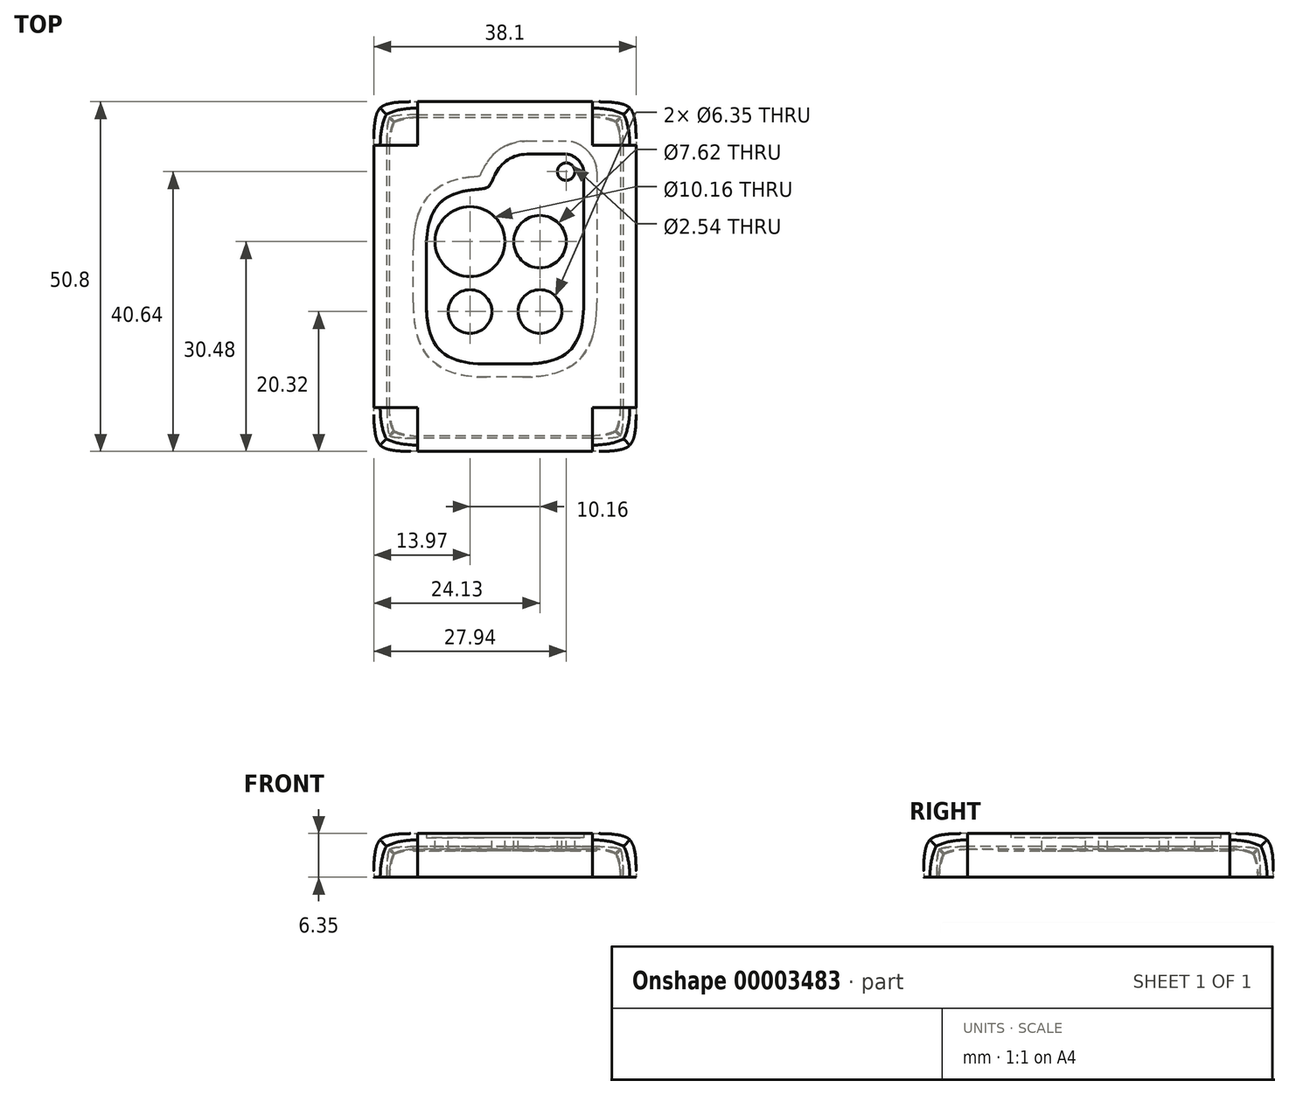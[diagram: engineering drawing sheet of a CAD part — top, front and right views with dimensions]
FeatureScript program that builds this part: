
annotation { "Feature Type Name" : "Feature", "Feature Type Description" : "" }
export const myFeature = defineFeature(function(context is Context, id is Id, definition is map)
    precondition{}
    {
        {
            var Q0;
            Q0=qCreatedBy(makeId("Top.planeOp"),FACE);
            var sketch = newSketch(context, id + "F0", { "sketchPlane" : qUnion([Q0])});
            skLineSegment(sketch, "E0.rect.bottom", {"start": v(19.05, 25.4) * mm, "end": v(-19.05, 25.4) * mm});
            skLineSegment(sketch, "E0.rect.top", {"start": v(19.05, -25.4) * mm, "end": v(-19.05, -25.4) * mm});
            skLineSegment(sketch, "E0.rect.left", {"start": v(19.05, 25.4) * mm, "end": v(19.05, -25.4) * mm});
            skLineSegment(sketch, "E0.rect.right", {"start": v(-19.05, 25.4) * mm, "end": v(-19.05, -25.4) * mm});
            skPoint(sketch, "E0.rect.middle", {"position": v(0, 0) * mm});
            skSolve(sketch);
        }
        {
            var Q0;
            Q0 = qSketchRegion(id + "F0", true);
            extrude(context, id + "F1", {"entities" : qUnion([Q0]), "depth" : 6.35 * mm});
        }
        {
            var Q0;
            Q0=makeQuery(id+"F1.opExtrude","SWEPT_EDGE",EDGE,{"disambiguationData":[OSD([sQuery(id+"F0.wireOp",EDGE,"E0.rect.top"),sQuery(id+"F0.wireOp",EDGE,"E0.rect.right")])]});
            var Q1;
            Q1=makeQuery(id+"F1.opExtrude","SWEPT_EDGE",EDGE,{"disambiguationData":[OSD([sQuery(id+"F0.wireOp",EDGE,"E0.rect.top"),sQuery(id+"F0.wireOp",EDGE,"E0.rect.left")])]});
            var Q2;
            Q2=makeQuery(id+"F1.opExtrude","SWEPT_EDGE",EDGE,{"disambiguationData":[OSD([sQuery(id+"F0.wireOp",EDGE,"E0.rect.bottom"),sQuery(id+"F0.wireOp",EDGE,"E0.rect.left")])]});
            var Q3;
            Q3=makeQuery(id+"F1.opExtrude","SWEPT_EDGE",EDGE,{"disambiguationData":[OSD([sQuery(id+"F0.wireOp",EDGE,"E0.rect.bottom"),sQuery(id+"F0.wireOp",EDGE,"E0.rect.right")])]});
            var Q4;
            Q4=makeQuery(id+"F1.opExtrude","CAP_FACE",FACE,{"disambiguationData":[OSD([sQuery(id+"F0.wireOp",EDGE,"E0.rect.bottom"),sQuery(id+"F0.wireOp",EDGE,"E0.rect.top"),sQuery(id+"F0.wireOp",EDGE,"E0.rect.left"),sQuery(id+"F0.wireOp",EDGE,"E0.rect.right")])],"isStart":false});
            fillet(context, id + "F2", {"entities" : qUnion([Q0, Q1, Q2, Q3, Q4]), "radius" : 6.35 * mm, "tangentPropagation" : true, "rho" : 0.71, "crossSection" : FilletCrossSection.CONIC, "allowEdgeOverflow" : false});
        }
        {
            var Q0;
            Q0=makeQuery(id+"F1.opExtrude","CAP_FACE",FACE,{"disambiguationData":[OSD([sQuery(id+"F0.wireOp",EDGE,"E0.rect.bottom"),sQuery(id+"F0.wireOp",EDGE,"E0.rect.top"),sQuery(id+"F0.wireOp",EDGE,"E0.rect.left"),sQuery(id+"F0.wireOp",EDGE,"E0.rect.right")])],"isStart":false});
            var sketch = newSketch(context, id + "F3", { "sketchPlane" : qUnion([Q0])});
            skLineSegment(sketch, "E1.rect.bottom", {"start": v(-1.9, 12.7) * mm, "end": v(-11.43, 12.7) * mm});
            skLineSegment(sketch, "E1.rect.top", {"start": v(11.43, -12.7) * mm, "end": v(-11.43, -12.7) * mm});
            skLineSegment(sketch, "E1.rect.left", {"start": v(11.43, 12.7) * mm, "end": v(11.43, -12.7) * mm});
            skLineSegment(sketch, "E1.rect.right", {"start": v(-11.43, 12.7) * mm, "end": v(-11.43, -12.7) * mm});
            skPoint(sketch, "E1.rect.middle", {"position": v(0, 0) * mm});
            skArc(sketch, "E2", {"start": v(3.17, 17.78) * mm, "mid": v(-0.42, 16.3) * mm, "end": v(-1.9, 12.7) * mm});
            skLineSegment(sketch, "E3", {"start": v(11.43, 12.7) * mm, "end": v(11.43, 17.78) * mm});
            skLineSegment(sketch, "E4", {"start": v(11.43, 17.78) * mm, "end": v(3.17, 17.78) * mm});
            skSolve(sketch);
        }
        {
            var Q0;
            Q0=makeQuery(id+"F3.imprint","IMPRINT",FACE,{"disambiguationData":[TD([[makeQuery(id+"F3.imprint","IMPRINT",EDGE,{"derivedFrom":sQuery(id+"F3.wireOp",EDGE,"E1.rect.bottom")}),1.0]])]});
            extrude(context, id + "F4", {"entities" : qUnion([Q0]), "operationType" : NewBodyOperationType.REMOVE, "oppositeDirection" : true, "depth" : 0.64 * mm});
        }
        {
            var Q0;
            Q0=makeQuery(id+"F4.boolean.opBoolean","COPY",EDGE,{"derivedFrom":makeQuery(id+"F4.opExtrude","SWEPT_EDGE",EDGE,{"disambiguationData":[OSD([sQuery(id+"F3.wireOp",EDGE,"E1.rect.bottom"),sQuery(id+"F3.wireOp",EDGE,"E1.rect.right")])]})});
            var Q1;
            Q1=makeQuery(id+"F4.boolean.opBoolean","COPY",EDGE,{"derivedFrom":makeQuery(id+"F4.opExtrude","SWEPT_EDGE",EDGE,{"disambiguationData":[OSD([sQuery(id+"F3.wireOp",EDGE,"E1.rect.top"),sQuery(id+"F3.wireOp",EDGE,"E1.rect.right")])]})});
            var Q2;
            Q2=makeQuery(id+"F4.boolean.opBoolean","COPY",EDGE,{"derivedFrom":makeQuery(id+"F4.opExtrude","SWEPT_EDGE",EDGE,{"disambiguationData":[OSD([sQuery(id+"F3.wireOp",EDGE,"E1.rect.top"),sQuery(id+"F3.wireOp",EDGE,"E1.rect.left")])]})});
            fillet(context, id + "F5", {"entities" : qUnion([Q0, Q1, Q2]), "radius" : 8.9 * mm, "tangentPropagation" : true, "rho" : 0.55, "crossSection" : FilletCrossSection.CONIC, "allowEdgeOverflow" : false});
        }
        {
            var Q0;
            Q0=makeQuery(id+"F4.boolean.opBoolean","COPY",EDGE,{"derivedFrom":makeQuery(id+"F4.opExtrude","SWEPT_EDGE",EDGE,{"disambiguationData":[OSD([sQuery(id+"F3.wireOp",EDGE,"E3"),sQuery(id+"F3.wireOp",EDGE,"E4")])]})});
            fillet(context, id + "F6", {"entities" : qUnion([Q0]), "radius" : 2.54 * mm, "tangentPropagation" : true, "rho" : 0.35, "crossSection" : FilletCrossSection.CONIC, "allowEdgeOverflow" : false});
        }
        {
            var Q0;
            Q0=makeQuery(id+"F4.boolean.opBoolean","COPY",EDGE,{"derivedFrom":makeQuery(id+"F4.opExtrude","SWEPT_EDGE",EDGE,{"disambiguationData":[OSD([sQuery(id+"F3.wireOp",EDGE,"E1.rect.bottom"),sQuery(id+"F3.wireOp",EDGE,"E2")])]})});
            fillet(context, id + "F7", {"entities" : qUnion([Q0]), "radius" : 3.8 * mm, "tangentPropagation" : true, "rho" : 0.8, "crossSection" : FilletCrossSection.CONIC, "allowEdgeOverflow" : false});
        }
        {
            var Q0;
            Q0=makeQuery(id+"F1.opExtrude","CAP_FACE",FACE,{"disambiguationData":[OSD([sQuery(id+"F0.wireOp",EDGE,"E0.rect.bottom"),sQuery(id+"F0.wireOp",EDGE,"E0.rect.top"),sQuery(id+"F0.wireOp",EDGE,"E0.rect.left"),sQuery(id+"F0.wireOp",EDGE,"E0.rect.right")])],"isStart":true});
            shell(context, id + "F8", {"entities" : qUnion([Q0]), "thickness" : 1.9 * mm});
        }
        {
            var Q0;
            Q0=makeQuery(id+"F4.boolean.opBoolean","COPY",FACE,{"derivedFrom":makeQuery(id+"F4.opExtrude","CAP_FACE",FACE,{"disambiguationData":[OSD([sQuery(id+"F3.wireOp",EDGE,"E1.rect.bottom"),sQuery(id+"F3.wireOp",EDGE,"E1.rect.top"),sQuery(id+"F3.wireOp",EDGE,"E1.rect.left"),sQuery(id+"F3.wireOp",EDGE,"E1.rect.right"),sQuery(id+"F3.wireOp",EDGE,"E2"),sQuery(id+"F3.wireOp",EDGE,"E3"),sQuery(id+"F3.wireOp",EDGE,"E4")])],"isStart":false})});
            var sketch = newSketch(context, id + "F9", { "sketchPlane" : qUnion([Q0])});
            skCircle(sketch, "E5", {"center": v(8.89, 15.24) * mm, "radius": 1.27 * mm});
            skCircle(sketch, "E6", {"center": v(-5.08, 5.08) * mm, "radius": 5.08 * mm});
            skCircle(sketch, "E7", {"center": v(5.08, 5.08) * mm, "radius": 3.81 * mm});
            skCircle(sketch, "E8", {"center": v(5.08, -5.08) * mm, "radius": 3.18 * mm});
            skCircle(sketch, "E9", {"center": v(-5.08, -5.08) * mm, "radius": 3.18 * mm});
            skLineSegment(sketch, "E10", {"start": v(-5.08, -5.08) * mm, "end": v(-5.08, 5.08) * mm, "construction": true});
            skLineSegment(sketch, "E11", {"start": v(5.08, 5.08) * mm, "end": v(5.08, -5.08) * mm, "construction": true});
            skLineSegment(sketch, "E12", {"start": v(5.08, 0) * mm, "end": v(-5.08, 0) * mm, "construction": true});
            skSolve(sketch);
        }
        {
            var Q0;
            Q0 = qSketchRegion(id + "F9", true);
            extrude(context, id + "F10", {"entities" : qUnion([Q0]), "operationType" : NewBodyOperationType.REMOVE, "endBound" : BoundingType.THROUGH_ALL, "oppositeDirection" : true, "depth" : 25.4 * mm});
        }
    });
